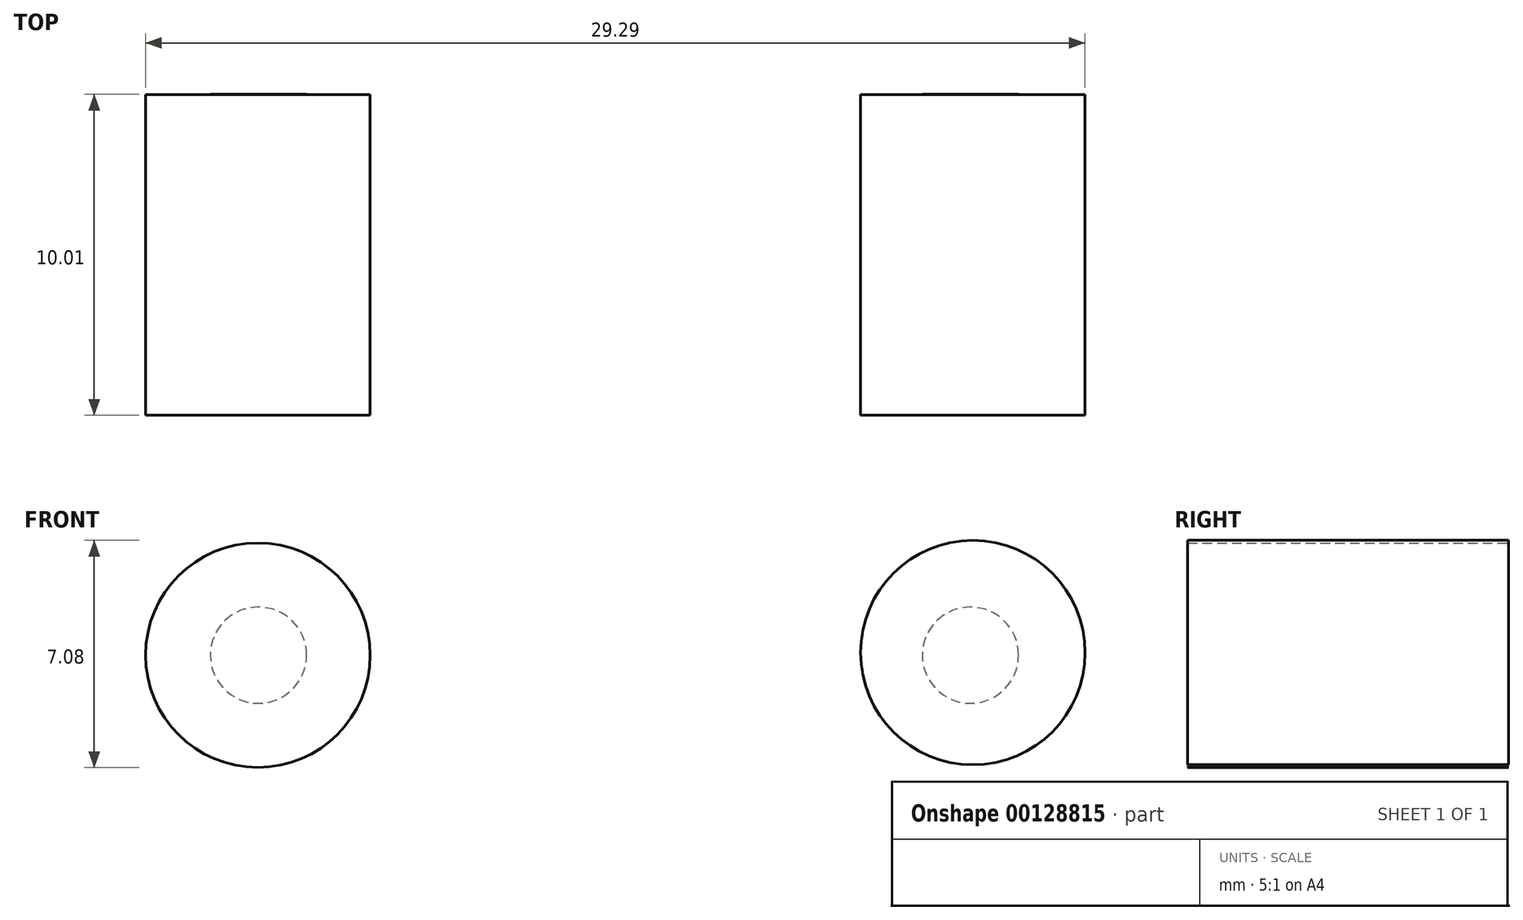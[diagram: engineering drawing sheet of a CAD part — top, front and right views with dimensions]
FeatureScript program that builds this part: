
annotation { "Feature Type Name" : "Feature", "Feature Type Description" : "" }
export const myFeature = defineFeature(function(context is Context, id is Id, definition is map)
    precondition{}
    {
        {
            var Q0;
            Q0=qCreatedBy(makeId("Front.planeOp"),FACE);
            var sketch = newSketch(context, id + "F0", { "sketchPlane" : qUnion([Q0])});
            skCircle(sketch, "E0", {"center": v(-10.98, 0) * mm, "radius": 3.5 * mm});
            skCircle(sketch, "E1", {"center": v(11.31, 0.08) * mm, "radius": 3.5 * mm});
            skSolve(sketch);
        }
        {
            var Q0;
            Q0 = qSketchRegion(id + "F0", true);
            extrude(context, id + "F1", {"entities" : qUnion([Q0]), "depth" : 10 * mm});
        }
        {
            var Q0;
            Q0=qCreatedBy(makeId("Front.planeOp"),FACE);
            var sketch = newSketch(context, id + "F2", { "sketchPlane" : qUnion([Q0])});
            skCircle(sketch, "E2", {"center": v(-10.96, 0) * mm, "radius": 1.5 * mm});
            skCircle(sketch, "E3", {"center": v(11.24, 0) * mm, "radius": 1.5 * mm});
            skSolve(sketch);
        }
        {
            var Q0;
            Q0 = qSketchRegion(id + "F2", true);
            extrude(context, id + "F3", {"entities" : qUnion([Q0]), "oppositeDirection" : true, "depth" : 0.01 * mm});
        }
    });
